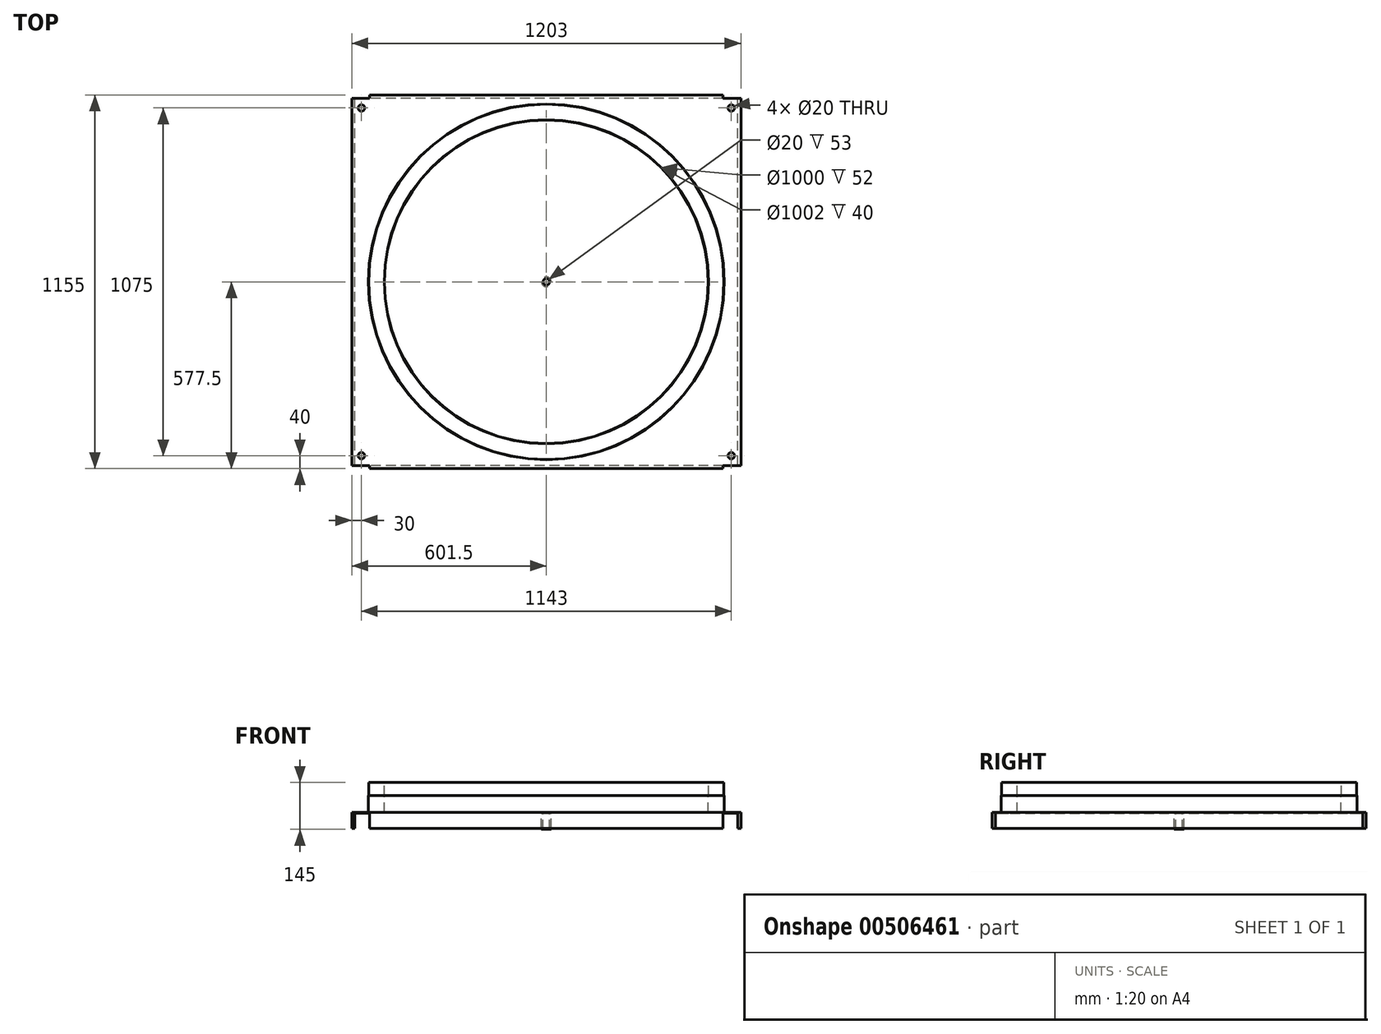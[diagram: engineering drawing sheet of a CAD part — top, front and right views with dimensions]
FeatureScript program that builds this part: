
annotation { "Feature Type Name" : "Feature", "Feature Type Description" : "" }
export const myFeature = defineFeature(function(context is Context, id is Id, definition is map)
    precondition{}
    {
        {
            var Q0;
            Q0=qCreatedBy(makeId("Front.planeOp"),FACE);
            var sketch = newSketch(context, id + "F0", { "sketchPlane" : qUnion([Q0])});
            skLineSegment(sketch, "E0", {"start": v(0, 74.87) * mm, "end": v(0, -73.71) * mm, "construction": true});
            skLineSegment(sketch, "E1", {"start": v(0, 374.84) * mm, "end": v(0, 1) * mm, "construction": true});
            skLineSegment(sketch, "E2", {"start": v(-500, 3) * mm, "end": v(-500, 55) * mm});
            skLineSegment(sketch, "E3", {"start": v(-500, 55) * mm, "end": v(-501, 55) * mm});
            skLineSegment(sketch, "E4", {"start": v(-501, 55) * mm, "end": v(-501, 95) * mm});
            skLineSegment(sketch, "E5", {"start": v(-501, 95) * mm, "end": v(-549, 95) * mm});
            skLineSegment(sketch, "E6", {"start": v(-549, 95) * mm, "end": v(-549, 55) * mm});
            skLineSegment(sketch, "E7", {"start": v(-549, 55) * mm, "end": v(-550, 55) * mm});
            skLineSegment(sketch, "E8", {"start": v(-550, 55) * mm, "end": v(-550, 3) * mm});
            skLineSegment(sketch, "E9", {"start": v(-550, 3) * mm, "end": v(-500, 3) * mm});
            skLineSegment(sketch, "E10.trimOffspring", {"start": v(0, 0) * mm, "end": v(0, -528.94) * mm, "construction": true});
            skLineSegment(sketch, "E11.bottom", {"start": v(-550, 3) * mm, "end": v(-10, 3) * mm});
            skLineSegment(sketch, "E11.top", {"start": v(-550, 0) * mm, "end": v(-10, 0) * mm});
            skLineSegment(sketch, "E11.left", {"start": v(-550, 3) * mm, "end": v(-550, 0) * mm});
            skLineSegment(sketch, "E11.right", {"start": v(-10, 3) * mm, "end": v(-10, 0) * mm});
            skSolve(sketch);
        }
        {
            var Q0;
            Q0=qSketchRegion(id+"F0",true);
            var Q1;
            Q1=sQuery(id+"F0.wireOp",EDGE,"E1");
            revolve(context, id + "F1", {"entities" : qUnion([Q0]), "axis" : qUnion([Q1]), "revolveType" : RevolveType.FULL});
        }
        {
            var Q0;
            Q0=qCreatedBy(makeId("Top.planeOp"),FACE);
            var sketch = newSketch(context, id + "F2", { "sketchPlane" : qUnion([Q0])});
            skLineSegment(sketch, "E12.bottom", {"start": v(601.5, 567.5) * mm, "end": v(-601.5, 567.5) * mm});
            skLineSegment(sketch, "E12.top", {"start": v(601.5, -567.5) * mm, "end": v(-601.5, -567.5) * mm});
            skLineSegment(sketch, "E12.left", {"start": v(601.5, 567.5) * mm, "end": v(601.5, -567.5) * mm});
            skLineSegment(sketch, "E12.right", {"start": v(-601.5, 567.5) * mm, "end": v(-601.5, -567.5) * mm});
            skPoint(sketch, "E12.middle", {"position": v(0, 0) * mm});
            skCircle(sketch, "E13.0", {"center": v(0, 0) * mm, "radius": 501 * mm});
            skCircle(sketch, "E14.0", {"center": v(0, 0) * mm, "radius": 500 * mm});
            skLineSegment(sketch, "E15", {"start": v(0, 0) * mm, "end": v(0, 773.78) * mm, "construction": true});
            skLineSegment(sketch, "E16", {"start": v(0, 0) * mm, "end": v(1007.48, 0) * mm, "construction": true});
            skCircle(sketch, "E17", {"center": v(571.5, 537.5) * mm, "radius": 10 * mm});
            skCircle(sketch, "E18.MirrorC", {"center": v(-571.5, 537.5) * mm, "radius": 10 * mm});
            skCircle(sketch, "E19.MirrorC", {"center": v(571.5, -537.5) * mm, "radius": 10 * mm});
            skCircle(sketch, "E20.MirrorC", {"center": v(-571.5, -537.5) * mm, "radius": 10 * mm});
            skSolve(sketch);
        }
        {
            var Q0;
            Q0=qSketchRegion(id+"F2",true);
            extrude(context, id + "F3", {"entities" : qUnion([Q0]), "operationType" : NewBodyOperationType.ADD, "depth" : 3 * mm, "offsetDistance" : 25 * mm});
        }
        {
            var Q0;
            Q0=makeQuery(id+"F3.opExtrude","CAP_FACE",FACE,{"disambiguationData":[OSD([sQuery(id+"F2.wireOp",EDGE,"E12.bottom"),sQuery(id+"F2.wireOp",EDGE,"E12.top"),sQuery(id+"F2.wireOp",EDGE,"E12.left"),sQuery(id+"F2.wireOp",EDGE,"E12.right"),sQuery(id+"F2.wireOp",EDGE,"E14.0"),sQuery(id+"F2.wireOp",EDGE,"E17"),sQuery(id+"F2.wireOp",EDGE,"E18.MirrorC"),sQuery(id+"F2.wireOp",EDGE,"E19.MirrorC"),sQuery(id+"F2.wireOp",EDGE,"E20.MirrorC")])],"isStart":false});
            var sketch = newSketch(context, id + "F4", { "sketchPlane" : qUnion([Q0])});
            skLineSegment(sketch, "E21", {"start": v(0, 0) * mm, "end": v(-1098.02, 0) * mm, "construction": true});
            skLineSegment(sketch, "E22", {"start": v(0, 0) * mm, "end": v(0, -1084.2) * mm, "construction": true});
            skLineSegment(sketch, "E23.bottom", {"start": v(546.5, -567.5) * mm, "end": v(-546.5, -567.5) * mm});
            skLineSegment(sketch, "E23.top", {"start": v(546.5, -577.5) * mm, "end": v(-546.5, -577.5) * mm});
            skLineSegment(sketch, "E23.left", {"start": v(546.5, -567.5) * mm, "end": v(546.5, -577.5) * mm});
            skLineSegment(sketch, "E23.right", {"start": v(-546.5, -567.5) * mm, "end": v(-546.5, -577.5) * mm});
            skLineSegment(sketch, "E24.bottom", {"start": v(-601.5, -567.5) * mm, "end": v(-591.5, -567.5) * mm});
            skLineSegment(sketch, "E24.top", {"start": v(-601.5, 567.5) * mm, "end": v(-591.5, 567.5) * mm});
            skLineSegment(sketch, "E24.left", {"start": v(-601.5, 567.5) * mm, "end": v(-601.5, -567.5) * mm});
            skLineSegment(sketch, "E24.right", {"start": v(-591.5, 567.5) * mm, "end": v(-591.5, -567.5) * mm});
            skLineSegment(sketch, "E25.MirrorCS", {"start": v(546.5, 567.5) * mm, "end": v(546.5, 577.5) * mm});
            skLineSegment(sketch, "E26.MirrorCS", {"start": v(-546.5, 567.5) * mm, "end": v(-546.5, 577.5) * mm});
            skLineSegment(sketch, "E27.MirrorCS", {"start": v(546.5, 577.5) * mm, "end": v(-546.5, 577.5) * mm});
            skLineSegment(sketch, "E28.MirrorCS", {"start": v(546.5, 567.5) * mm, "end": v(-546.5, 567.5) * mm});
            skLineSegment(sketch, "E29.MirrorCS", {"start": v(601.5, 567.5) * mm, "end": v(591.5, 567.5) * mm});
            skLineSegment(sketch, "E30.MirrorCS", {"start": v(601.5, -567.5) * mm, "end": v(591.5, -567.5) * mm});
            skLineSegment(sketch, "E31.MirrorCS", {"start": v(601.5, 567.5) * mm, "end": v(601.5, -567.5) * mm});
            skLineSegment(sketch, "E32.MirrorCS", {"start": v(591.5, 567.5) * mm, "end": v(591.5, -567.5) * mm});
            skLineSegment(sketch, "E33.MirrorCS", {"start": v(0, 0) * mm, "end": v(1098.02, 0) * mm, "construction": true});
            skSolve(sketch);
        }
        {
            var Q0;
            Q0=qSketchRegion(id+"F4",true);
            extrude(context, id + "F5", {"entities" : qUnion([Q0]), "operationType" : NewBodyOperationType.ADD, "oppositeDirection" : true, "depth" : 50 * mm, "offsetDistance" : 25 * mm});
        }
        {
            var Q0;
            Q0=makeQuery(id+"F3.boolean.opBoolean","MERGE",FACE,{"derivedFrom":[makeQuery(id+"F1.opRevolve","SWEPT_FACE",FACE,{"disambiguationData":[OSD([sQuery(id+"F0.wireOp",EDGE,"E11.top")])]}),makeQuery(id+"F3.opExtrude","CAP_FACE",FACE,{"disambiguationData":[OSD([sQuery(id+"F2.wireOp",EDGE,"E12.bottom"),sQuery(id+"F2.wireOp",EDGE,"E12.top"),sQuery(id+"F2.wireOp",EDGE,"E12.left"),sQuery(id+"F2.wireOp",EDGE,"E12.right"),sQuery(id+"F2.wireOp",EDGE,"E13.0"),sQuery(id+"F2.wireOp",EDGE,"E17"),sQuery(id+"F2.wireOp",EDGE,"E18.MirrorC"),sQuery(id+"F2.wireOp",EDGE,"E19.MirrorC"),sQuery(id+"F2.wireOp",EDGE,"E20.MirrorC")])],"isStart":false})]});
            var sketch = newSketch(context, id + "F6", { "sketchPlane" : qUnion([Q0])});
            skCircle(sketch, "E34.0", {"center": v(0, 0) * mm, "radius": 10 * mm});
            skCircle(sketch, "E35", {"center": v(0, 0) * mm, "radius": 15 * mm});
            skSolve(sketch);
        }
        {
            var Q0;
            Q0 = qSketchRegion(id + "F6", true);
            extrude(context, id + "F7", {"entities" : qUnion([Q0]), "operationType" : NewBodyOperationType.ADD, "depth" : 50 * mm, "offsetDistance" : 25 * mm});
        }
    });
